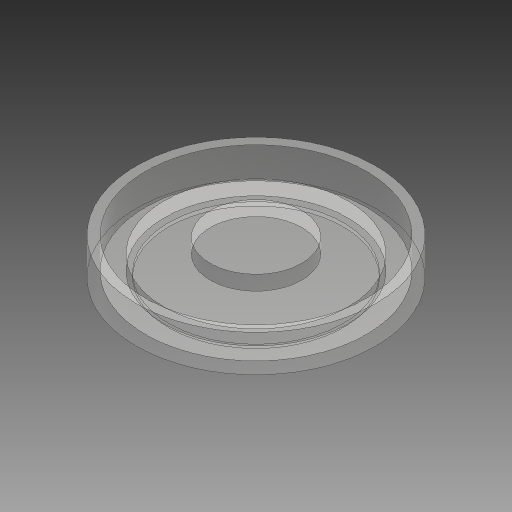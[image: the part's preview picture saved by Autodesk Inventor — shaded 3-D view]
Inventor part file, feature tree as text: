
AUTODESK INVENTOR PART (.ipt)
format: ipt  version: 2019 (Build 230136000, 136)  size: 122,368 bytes
history: native  units: mm
features: extrude x5, sketch x5
ambient origin geometry x8: Origin, YZ Plane, XZ Plane, XY Plane, X Axis, Y Axis, Z Axis, Center Point
bodies: Volumenkörper1 (feature_tree)
feature tree (10):
  extrude  "Extrusion1"  Depth=2.0mm
  extrude  "Extrusion2"  Depth=1.7mm TaperAngle=0.0deg
  extrude  "Extrusion3"  Depth=0.8mm TaperAngle=0.0deg
  extrude  "Extrusion4"  Depth=0.8mm
  extrude  "Extrusion5"  [1 undecoded]
  sketch  "Skizze1"  dims[d0=2.0mm d1=0.0mm d2=13.0mm]
  sketch  "Skizze2"  dims[d3=12.0mm d4=1.7mm d5=0.0mm]
  sketch  "Skizze3"  dims[d6=10.0mm d7=0.8mm d8=0.0mm]
  sketch  "Skizze4"  dims[d9=0.8mm d10=0.0mm d11=9.5mm]
  sketch  "Skizze5"  dims[d12=0.2mm d13=0.0mm]
note: 1 required parameter value undecoded (feature->parameter linkage not recoverable at this tier; creation-order binding heuristic only, values carry confidence <= 0.55)
